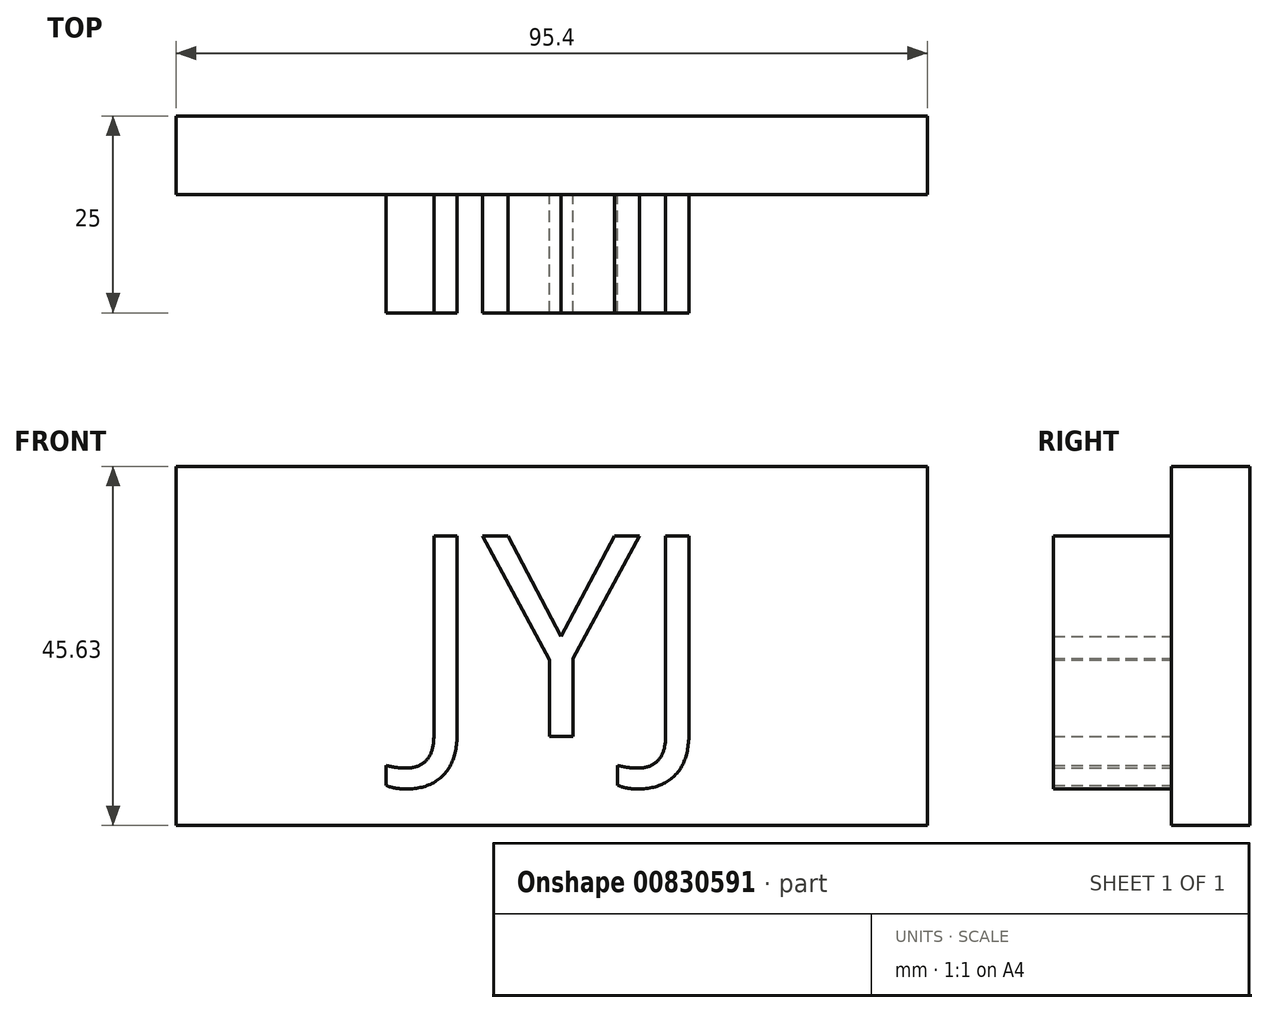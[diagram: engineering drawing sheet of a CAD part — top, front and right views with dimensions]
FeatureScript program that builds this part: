
annotation { "Feature Type Name" : "Feature", "Feature Type Description" : "" }
export const myFeature = defineFeature(function(context is Context, id is Id, definition is map)
    precondition{}
    {
        {
            var Q0;
            Q0=qCreatedBy(makeId("Front.planeOp"),FACE);
            var sketch = newSketch(context, id + "F0", { "sketchPlane" : qUnion([Q0])});
            skLineSegment(sketch, "E0.bottom", {"start": v(0, 0) * mm, "end": v(95.4, 0) * mm});
            skLineSegment(sketch, "E0.top", {"start": v(0, 45.63) * mm, "end": v(95.4, 45.63) * mm});
            skLineSegment(sketch, "E0.left", {"start": v(0, 0) * mm, "end": v(0, 45.63) * mm});
            skLineSegment(sketch, "E0.right", {"start": v(95.4, 0) * mm, "end": v(95.4, 45.63) * mm});
            skSolve(sketch);
        }
        {
            var Q0;
            Q0=makeQuery(id+"F0.imprint","IMPRINT",FACE,{"disambiguationData":[TD([[makeQuery(id+"F0.imprint","IMPRINT",EDGE,{"derivedFrom":sQuery(id+"F0.wireOp",EDGE,"E0.bottom")}),1.0]])]});
            extrude(context, id + "F1", {"entities" : qUnion([Q0]), "depth" : 10 * mm, "offsetDistance" : 25.4 * mm});
        }
        {
            var Q0;
            Q0=makeQuery(id+"F1.opExtrude","CAP_FACE",FACE,{"disambiguationData":[OSD([sQuery(id+"F0.wireOp",EDGE,"E0.bottom"),sQuery(id+"F0.wireOp",EDGE,"E0.top"),sQuery(id+"F0.wireOp",EDGE,"E0.left"),sQuery(id+"F0.wireOp",EDGE,"E0.right")])],"isStart":false});
            var sketch = newSketch(context, id + "F2", { "sketchPlane" : qUnion([Q0])});
            skText(sketch, "E1", { "text": "JYJ", "fontName": "OpenSans-Regular.ttf"});
            const initialGuessF2  = {"E1": [0.02942, 0.01134, 1, 0, 0.02563]};
            skSetInitialGuess(sketch, initialGuessF2);
            skSolve(sketch);
        }
        {
            var Q0;
            Q0 = qSketchRegion(id + "F2", true);
            extrude(context, id + "F3", {"entities" : qUnion([Q0]), "operationType" : NewBodyOperationType.ADD, "depth" : 15 * mm, "offsetDistance" : 25.4 * mm});
        }
    });
